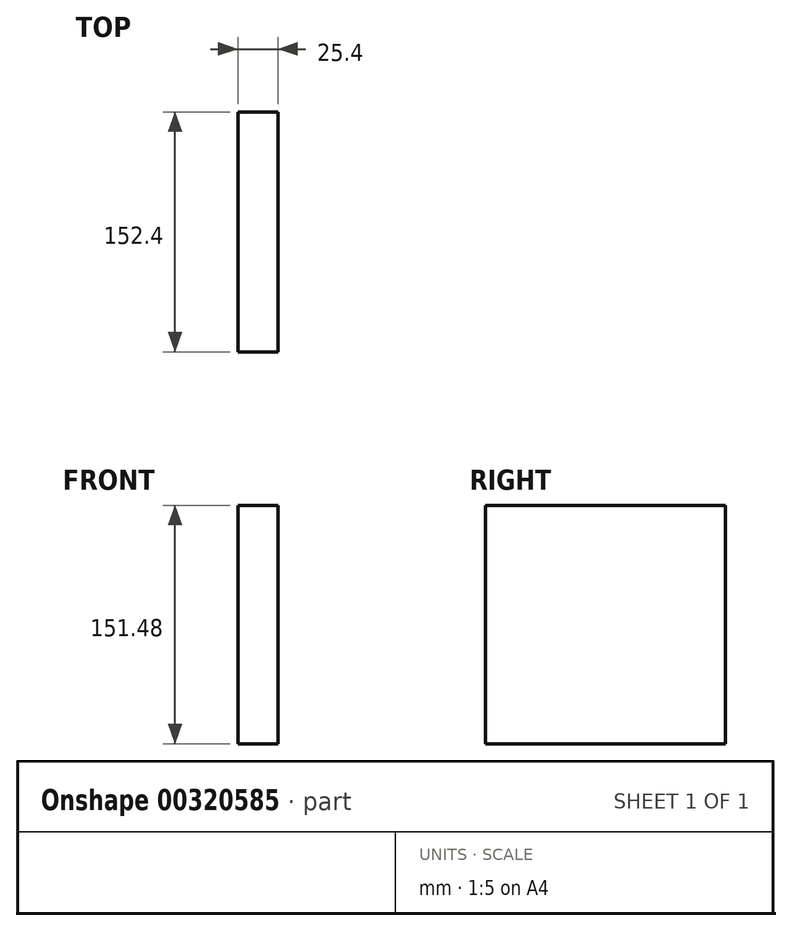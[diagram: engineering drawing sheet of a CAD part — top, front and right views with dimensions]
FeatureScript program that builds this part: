
annotation { "Feature Type Name" : "Feature", "Feature Type Description" : "" }
export const myFeature = defineFeature(function(context is Context, id is Id, definition is map)
    precondition{}
    {
        {
            var Q0;
            Q0=qCreatedBy(makeId("Right.planeOp"),FACE);
            var sketch = newSketch(context, id + "F0", { "sketchPlane" : qUnion([Q0])});
            skLineSegment(sketch, "E0.bottom", {"start": v(-76.2, 75.74) * mm, "end": v(76.2, 75.74) * mm});
            skLineSegment(sketch, "E0.top", {"start": v(-76.2, -75.74) * mm, "end": v(76.2, -75.74) * mm});
            skLineSegment(sketch, "E0.left", {"start": v(-76.2, 75.74) * mm, "end": v(-76.2, -75.74) * mm});
            skLineSegment(sketch, "E0.right", {"start": v(76.2, 75.74) * mm, "end": v(76.2, -75.74) * mm});
            skSolve(sketch);
        }
        {
            var Q0;
            Q0 = qSketchRegion(id + "F0", true);
            extrude(context, id + "F1", {"entities" : qUnion([Q0]), "depth" : 25.4 * mm});
        }
    });
